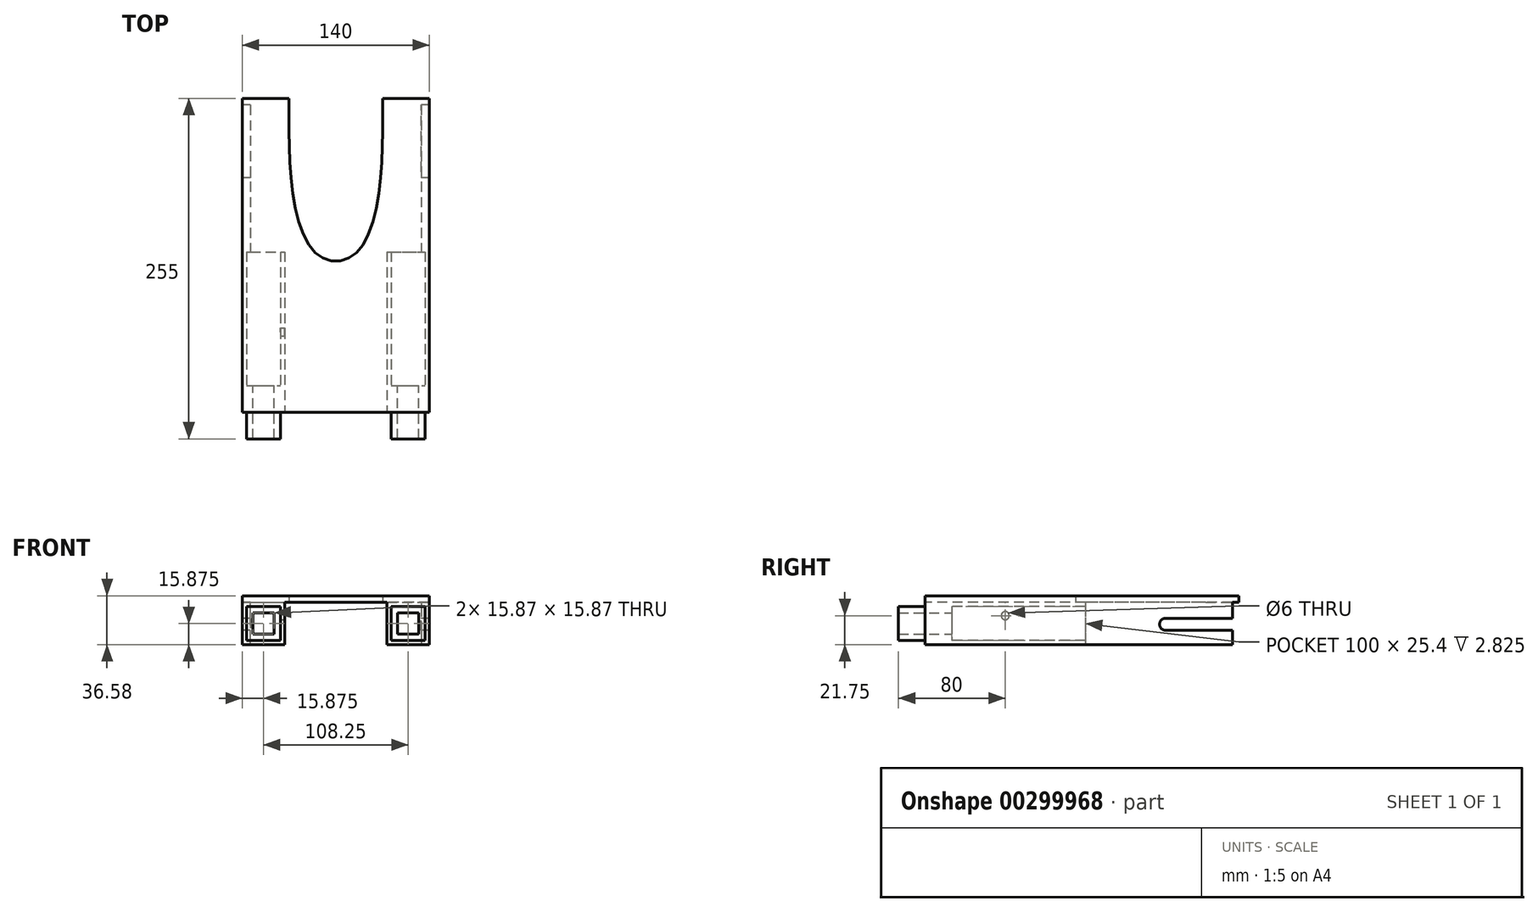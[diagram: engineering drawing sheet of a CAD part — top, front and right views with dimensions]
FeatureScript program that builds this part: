
annotation { "Feature Type Name" : "Feature", "Feature Type Description" : "" }
export const myFeature = defineFeature(function(context is Context, id is Id, definition is map)
    precondition{}
    {
        {
            var Q0;
            Q0=qCreatedBy(makeId("Top.planeOp"),FACE);
            var sketch = newSketch(context, id + "F0", { "sketchPlane" : qUnion([Q0])});
            skLineSegment(sketch, "E0.bottom", {"start": v(-66.5, 0) * mm, "end": v(73.5, 0) * mm});
            skLineSegment(sketch, "E0.top", {"start": v(-66.5, 110) * mm, "end": v(73.5, 110) * mm});
            skLineSegment(sketch, "E0.left", {"start": v(-66.5, 0) * mm, "end": v(-66.5, 110) * mm});
            skLineSegment(sketch, "E0.right", {"start": v(73.5, 0) * mm, "end": v(73.5, 110) * mm});
            skLineSegment(sketch, "E1", {"start": v(-66.5, 110) * mm, "end": v(-66.5, 210) * mm});
            skLineSegment(sketch, "E2", {"start": v(-66.5, 210) * mm, "end": v(-31.5, 210) * mm});
            skLineSegment(sketch, "E3", {"start": v(73.5, 110) * mm, "end": v(73.5, 210) * mm});
            skLineSegment(sketch, "E4", {"start": v(73.5, 210) * mm, "end": v(38.5, 210) * mm});
            skFitSpline(sketch, "E5", {"points": [v(-31.5, 210) * mm, v(-12.5, 120) * mm, v(19.5, 120) * mm, v(38.5, 210) * mm], "startDerivative": vector(0, -248.62) * mm, "endDerivative": vector(0, 248.62) * mm});
            skLineSegment(sketch, "E6.top", {"start": v(-66.5, 235) * mm, "end": v(-31.5, 235) * mm});
            skLineSegment(sketch, "E6.left", {"start": v(-66.5, 210) * mm, "end": v(-66.5, 235) * mm});
            skLineSegment(sketch, "E6.right", {"start": v(-31.5, 210) * mm, "end": v(-31.5, 235) * mm});
            skLineSegment(sketch, "E7.top", {"start": v(73.5, 235) * mm, "end": v(38.5, 235) * mm});
            skLineSegment(sketch, "E7.left", {"start": v(73.5, 210) * mm, "end": v(73.5, 235) * mm});
            skLineSegment(sketch, "E7.right", {"start": v(38.5, 210) * mm, "end": v(38.5, 235) * mm});
            skSolve(sketch);
        }
        {
            var Q0;
            Q0 = qSketchRegion(id + "F0", true);
            extrude(context, id + "F1", {"entities" : qUnion([Q0]), "depth" : 4.83 * mm, "offsetDistance" : 25 * mm});
        }
        {
            var Q0;
            Q0=makeQuery(id+"F1.opExtrude","SWEPT_FACE",FACE,{"disambiguationData":[OSD([sQuery(id+"F0.wireOp",EDGE,"E0.bottom")])]});
            var sketch = newSketch(context, id + "F2", { "sketchPlane" : qUnion([Q0])});
            skLineSegment(sketch, "E8.bottom", {"start": v(-66.5, 0) * mm, "end": v(-34.75, 0) * mm});
            skLineSegment(sketch, "E8.top", {"start": v(-66.5, -31.75) * mm, "end": v(-34.75, -31.75) * mm});
            skLineSegment(sketch, "E8.left", {"start": v(-66.5, 0) * mm, "end": v(-66.5, -31.75) * mm});
            skLineSegment(sketch, "E8.right", {"start": v(-34.75, 0) * mm, "end": v(-34.75, -31.75) * mm});
            skLineSegment(sketch, "E9.bottom", {"start": v(73.5, 0) * mm, "end": v(41.75, 0) * mm});
            skLineSegment(sketch, "E9.top", {"start": v(73.5, -31.75) * mm, "end": v(41.75, -31.75) * mm});
            skLineSegment(sketch, "E9.left", {"start": v(73.5, 0) * mm, "end": v(73.5, -31.75) * mm});
            skLineSegment(sketch, "E9.right", {"start": v(41.75, 0) * mm, "end": v(41.75, -31.75) * mm});
            skLineSegment(sketch, "E10.bottom", {"start": v(-63.33, -3.17) * mm, "end": v(-37.93, -3.17) * mm});
            skLineSegment(sketch, "E10.top", {"start": v(-63.33, -28.57) * mm, "end": v(-37.93, -28.57) * mm});
            skLineSegment(sketch, "E10.left", {"start": v(-63.33, -3.17) * mm, "end": v(-63.33, -28.57) * mm});
            skLineSegment(sketch, "E10.right", {"start": v(-37.93, -3.17) * mm, "end": v(-37.93, -28.57) * mm});
            skLineSegment(sketch, "E11.bottom", {"start": v(44.92, -3.18) * mm, "end": v(70.33, -3.17) * mm});
            skLineSegment(sketch, "E11.top", {"start": v(44.92, -28.58) * mm, "end": v(70.33, -28.58) * mm});
            skLineSegment(sketch, "E11.left", {"start": v(44.92, -3.18) * mm, "end": v(44.92, -28.58) * mm});
            skLineSegment(sketch, "E11.right", {"start": v(70.33, -3.17) * mm, "end": v(70.33, -28.58) * mm});
            skSolve(sketch);
        }
        {
            var Q0;
            Q0 = qSketchRegion(id + "F2", true);
            extrude(context, id + "F3", {"entities" : qUnion([Q0]), "operationType" : NewBodyOperationType.ADD, "oppositeDirection" : true, "depth" : 120 * mm});
        }
        {
            var Q0;
            Q0=makeQuery(id+"F3.opExtrude","CAP_FACE",FACE,{"disambiguationData":[OSD([sQuery(id+"F2.wireOp",EDGE,"E9.bottom"),sQuery(id+"F2.wireOp",EDGE,"E9.top"),sQuery(id+"F2.wireOp",EDGE,"E9.left"),sQuery(id+"F2.wireOp",EDGE,"E9.right"),sQuery(id+"F2.wireOp",EDGE,"E11.bottom"),sQuery(id+"F2.wireOp",EDGE,"E11.top"),sQuery(id+"F2.wireOp",EDGE,"E11.left"),sQuery(id+"F2.wireOp",EDGE,"E11.right")])],"isStart":false});
            var sketch = newSketch(context, id + "F4", { "sketchPlane" : qUnion([Q0])});
            skPoint(sketch, "E12.oppositeSnap0", {"position": v(-70.33, -15.88) * mm});
            skLineSegment(sketch, "E12.bottom", {"start": v(-73.5, 0) * mm, "end": v(-56, 0) * mm});
            skLineSegment(sketch, "E12.top", {"start": v(-73.5, -31.75) * mm, "end": v(-70.33, -31.75) * mm});
            skLineSegment(sketch, "E12.left", {"start": v(-73.5, 0) * mm, "end": v(-73.5, -31.75) * mm});
            skLineSegment(sketch, "E13.bottom", {"start": v(56, -31.75) * mm, "end": v(66.5, -31.75) * mm});
            skLineSegment(sketch, "E13.top", {"start": v(56, 0) * mm, "end": v(66.5, 0) * mm});
            skLineSegment(sketch, "E13.right", {"start": v(66.5, -31.75) * mm, "end": v(66.5, 0) * mm});
            skLineSegment(sketch, "E14", {"start": v(60.5, -31.75) * mm, "end": v(60.5, 0) * mm});
            skLineSegment(sketch, "E15", {"start": v(-67.5, 0) * mm, "end": v(-67.5, -31.75) * mm});
            skSolve(sketch);
        }
        {
            var Q0;
            Q0 = qSketchRegion(id + "F4", true);
            var Q1;
            {var subQ5=makeQuery(id+"F3.opExtrude","CAP_EDGE",EDGE,{"disambiguationData":[OSD([sQuery(id+"F2.wireOp",EDGE,"E11.right")])],"isStart":false});Q1=makeQuery(id+"F4.imprint","IMPRINT",FACE,{"disambiguationData":[TD([[makeQuery(id+"F4.imprint","IMPRINT",EDGE,{"derivedFrom":subQ5}),1.0]])]});}
            var Q2;
            {var subQ6=sQuery(id+"F4.wireOp",EDGE,"E12.top");Q2=makeQuery(id+"F4.imprint","IMPRINT",FACE,{"disambiguationData":[TD([[makeQuery(id+"F4.imprint","IMPRINT",EDGE,{"derivedFrom":subQ6}),1.0]])]});}
            extrude(context, id + "F5", {"entities" : qUnion([Q0, Q1, Q2]), "operationType" : NewBodyOperationType.ADD, "depth" : 110 * mm, "offsetDistance" : 25 * mm});
        }
        {
            var Q0;
            {var subQ0=sQuery(id+"F2.wireOp",EDGE,"E8.right");Q0=makeQuery(id+"FrnK0tPHe9QpJH6_1.boolean.opBoolean","MERGE",FACE,{"derivedFrom":[makeQuery(id+"F3.opExtrude","SWEPT_FACE",FACE,{"disambiguationData":[OSD([subQ0])]}),makeQuery(id+"FrnK0tPHe9QpJH6_1.opExtrude","SWEPT_FACE",FACE,{"disambiguationData":[OSD([subQ0])]})]});}
            var sketch = newSketch(context, id + "F6", { "sketchPlane" : qUnion([Q0])});
            skCircle(sketch, "E16", {"center": v(60, -10) * mm, "radius": 3 * mm});
            skSolve(sketch);
        }
        {
            var Q0;
            Q0 = qSketchRegion(id + "F6", true);
            extrude(context, id + "F7", {"entities" : qUnion([Q0]), "operationType" : NewBodyOperationType.REMOVE, "oppositeDirection" : true, "depth" : 10 * mm});
        }
        {
            var Q0;
            Q0=makeQuery(id+"F3.boolean.opBoolean","MERGE",FACE,{"derivedFrom":[makeQuery(id+"F1.opExtrude","SWEPT_FACE",FACE,{"disambiguationData":[OSD([sQuery(id+"F0.wireOp",EDGE,"E0.bottom")])]}),makeQuery(id+"F3.opExtrude","CAP_FACE",FACE,{"disambiguationData":[OSD([sQuery(id+"F2.wireOp",EDGE,"E8.bottom"),sQuery(id+"F2.wireOp",EDGE,"E8.top"),sQuery(id+"F2.wireOp",EDGE,"E8.left"),sQuery(id+"F2.wireOp",EDGE,"E8.right"),sQuery(id+"F2.wireOp",EDGE,"E10.bottom"),sQuery(id+"F2.wireOp",EDGE,"E10.top"),sQuery(id+"F2.wireOp",EDGE,"E10.left"),sQuery(id+"F2.wireOp",EDGE,"E10.right")])],"isStart":true}),makeQuery(id+"F3.opExtrude","CAP_FACE",FACE,{"disambiguationData":[OSD([sQuery(id+"F2.wireOp",EDGE,"E9.bottom"),sQuery(id+"F2.wireOp",EDGE,"E9.top"),sQuery(id+"F2.wireOp",EDGE,"E9.left"),sQuery(id+"F2.wireOp",EDGE,"E9.right"),sQuery(id+"F2.wireOp",EDGE,"E11.bottom"),sQuery(id+"F2.wireOp",EDGE,"E11.top"),sQuery(id+"F2.wireOp",EDGE,"E11.left"),sQuery(id+"F2.wireOp",EDGE,"E11.right")])],"isStart":true})]});
            var sketch = newSketch(context, id + "F8", { "sketchPlane" : qUnion([Q0])});
            skLineSegment(sketch, "E17.bottom", {"start": v(-63.33, -3.17) * mm, "end": v(-37.93, -3.17) * mm});
            skLineSegment(sketch, "E17.top", {"start": v(-63.33, -28.57) * mm, "end": v(-37.93, -28.57) * mm});
            skLineSegment(sketch, "E17.left", {"start": v(-63.33, -3.18) * mm, "end": v(-63.33, -28.57) * mm});
            skLineSegment(sketch, "E17.right", {"start": v(-37.93, -3.18) * mm, "end": v(-37.93, -28.57) * mm});
            skLineSegment(sketch, "E18.bottom", {"start": v(-58.56, -7.94) * mm, "end": v(-42.69, -7.94) * mm});
            skLineSegment(sketch, "E18.top", {"start": v(-58.56, -23.81) * mm, "end": v(-42.69, -23.81) * mm});
            skLineSegment(sketch, "E18.left", {"start": v(-58.56, -7.94) * mm, "end": v(-58.56, -23.81) * mm});
            skLineSegment(sketch, "E18.right", {"start": v(-42.69, -7.94) * mm, "end": v(-42.69, -23.81) * mm});
            skLineSegment(sketch, "E19.bottom", {"start": v(44.92, -3.18) * mm, "end": v(70.33, -3.18) * mm});
            skLineSegment(sketch, "E19.top", {"start": v(44.92, -28.58) * mm, "end": v(70.33, -28.58) * mm});
            skLineSegment(sketch, "E19.left", {"start": v(44.92, -3.18) * mm, "end": v(44.92, -28.58) * mm});
            skLineSegment(sketch, "E19.right", {"start": v(70.33, -3.18) * mm, "end": v(70.33, -28.58) * mm});
            skLineSegment(sketch, "E20.bottom", {"start": v(49.69, -7.94) * mm, "end": v(65.56, -7.94) * mm});
            skLineSegment(sketch, "E20.top", {"start": v(49.69, -23.81) * mm, "end": v(65.56, -23.81) * mm});
            skLineSegment(sketch, "E20.left", {"start": v(49.69, -7.94) * mm, "end": v(49.69, -23.81) * mm});
            skLineSegment(sketch, "E20.right", {"start": v(65.56, -7.94) * mm, "end": v(65.56, -23.81) * mm});
            skSolve(sketch);
        }
        {
            var Q0;
            Q0 = qSketchRegion(id + "F8", true);
            extrude(context, id + "F9", {"entities" : qUnion([Q0]), "operationType" : NewBodyOperationType.ADD, "endBound" : BoundingType.SYMMETRIC, "depth" : 40 * mm, "offsetDistance" : 25 * mm});
        }
        {
            var Q0;
            Q0=makeQuery(id+"F5.boolean.opBoolean","MERGE",FACE,{"derivedFrom":[makeQuery(id+"F3.opExtrude","SWEPT_FACE",FACE,{"disambiguationData":[OSD([sQuery(id+"F2.wireOp",EDGE,"E8.left")])]}),makeQuery(id+"F5.opExtrude","SWEPT_FACE",FACE,{"disambiguationData":[OSD([sQuery(id+"F4.wireOp",EDGE,"E13.right")])]})]});
            var sketch = newSketch(context, id + "F10", { "sketchPlane" : qUnion([Q0])});
            skCircle(sketch, "E21", {"center": v(-180, -16.5) * mm, "radius": 4.5 * mm});
            skLineSegment(sketch, "E22", {"start": v(-180, -16.5) * mm, "end": v(-180, -12) * mm});
            skLineSegment(sketch, "E23", {"start": v(-180, -12) * mm, "end": v(-230, -12) * mm});
            skLineSegment(sketch, "E24", {"start": v(-180, -16.5) * mm, "end": v(-180, -21) * mm});
            skLineSegment(sketch, "E25", {"start": v(-180, -21) * mm, "end": v(-230, -21) * mm});
            skSolve(sketch);
        }
        {
            var Q0;
            Q0 = qSketchRegion(id + "F10", true);
            var Q1;
            {var subQ0=sQuery(id+"F10.wireOp",EDGE,"E23");Q1=makeQuery(id+"F10.imprint","IMPRINT",FACE,{"disambiguationData":[TD([[makeQuery(id+"F10.imprint","IMPRINT",EDGE,{"derivedFrom":subQ0}),1.0]])]});}
            extrude(context, id + "F11", {"entities" : qUnion([Q0, Q1]), "operationType" : NewBodyOperationType.REMOVE, "oppositeDirection" : true, "depth" : 152 * mm, "offsetDistance" : 25 * mm});
        }
    });
